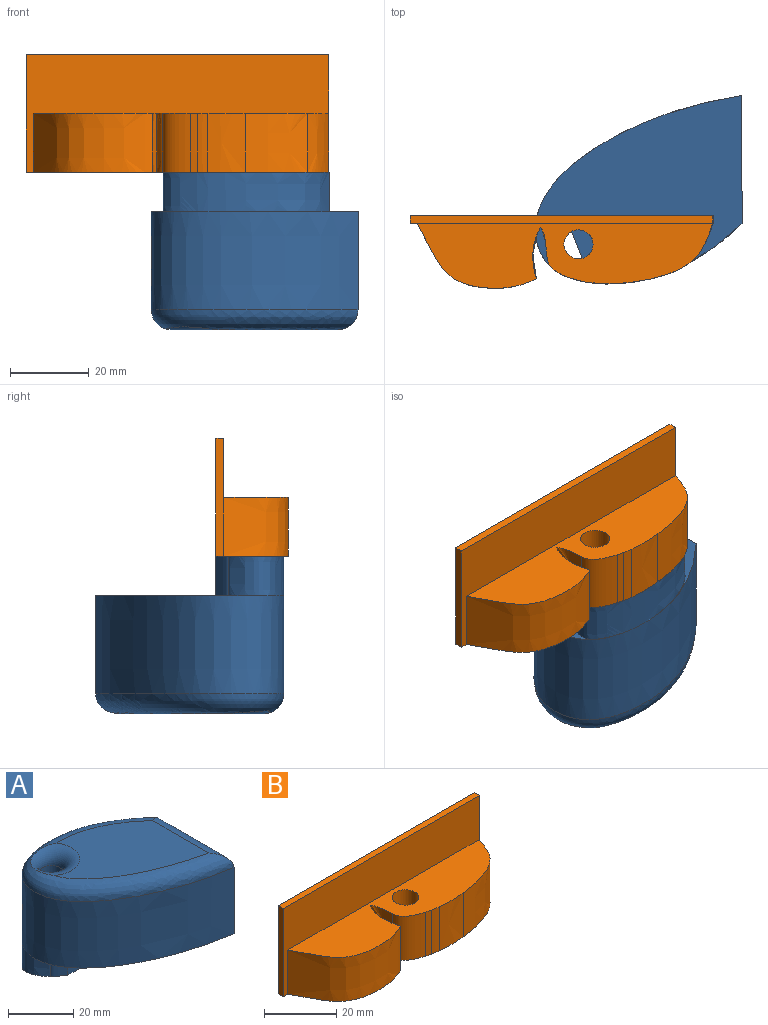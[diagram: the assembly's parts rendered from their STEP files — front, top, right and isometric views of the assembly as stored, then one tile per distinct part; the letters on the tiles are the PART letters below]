
ASSEMBLY  parts=2 mates=1
PART A: 18 faces, bbox 54.8x48.9x40 mm
  f0: plane 54.08x48.92mm, normal (0,0,-1), area 1219.3mm2, adj f1,f3,f4,f15,f16,f17
  f1: extruded ~42.09x15.25mm, area 596.5mm2, adj f0,f2,f10,f13,f14,f15,f16
  f2: plane 2.18x0.61mm, normal (0,0,-1), area 0mm2, adj f1,f4
  f3: plane 32.6x25mm, normal (1,0,0), area 815.1mm2, adj f0,f4,f8
  f4: extruded ~52.55x47.9mm, area 3277.6mm2, adj f0,f2,f3,f9,f10,f14
  f5: cylinder r=3.73mm len=25mm, axis (0,0,-1), area 585.4mm2, adj f7,f11
  f6: plane 42.11x36.98mm, normal (0,0,1), area 913.3mm2, adj f7,f8,f9
  f7: torus R=8.73mm, axis (0,0,1), area 227mm2, adj f5,f6,f9
  f8: cylinder r=5mm len=32.6mm, axis (0,-1,0), area 224.1mm2, adj f3,f6,f9
  f9: bspline ~53.26x47.91mm, area 944.3mm2, adj f4,f6,f7,f8
  f10: plane 2.77x0.58mm, normal (0,0,1), area 0mm2, adj f1,f4
  f11: plane 7.45x7.45mm, normal (0,0,1), area 0.3mm2, adj f5,f12
  f12: cylinder r=3.71mm len=10mm, axis (0,0,1), area 233.3mm2, adj f11,f13
  f13: plane 42.52x17.62mm, normal (0,0,-1), area 540.7mm2, adj f1,f12,f15,f16,f17
  f14: plane 5.89x3.33mm, normal (0,0,1), area 0.4mm2, adj f1,f4
  f15: extruded ~10x4.2mm, area 54.7mm2, adj f0,f1,f13,f17
  f16: plane 10x2mm, normal (1,0,0), area 20mm2, adj f0,f1,f13,f17
  f17: plane 34.25x10mm, normal (0,-1,0), area 342.5mm2, adj f0,f13,f15,f16
PART B: 20 faces, bbox 77x18.6x30 mm
  f0: plane 75.34x16.75mm, normal (0,0,1), area 899.1mm2, adj f1,f2,f3,f4,f5,f6,f7,f8
  f1: extruded ~15x0.02mm, area 0.5mm2, adj f0,f6,f13,f19
  f2: extruded ~30.34x16.47mm, area 581.8mm2, adj f0,f13,f14,f19
  f3: extruded ~15.9x15mm, area 255.1mm2, adj f0,f4,f11,f13
  f4: extruded ~15x9.61mm, area 167.4mm2, adj f0,f3,f13,f17
  f5: extruded ~15x0.1mm, area 1.5mm2, adj f0,f6,f13,f19
  f6: plane 15x8.85mm, normal (0,1,0), area 132.7mm2, adj f0,f1,f5,f13
  f7: extruded ~15x7.28mm, area 113.6mm2, adj f0,f8,f13,f14
  f8: extruded ~15x7.02mm, area 148.1mm2, adj f0,f7,f9,f13
  f9: extruded ~15x1.8mm, area 27.9mm2, adj f0,f8,f10,f13
  f10: extruded ~15x2.64mm, area 40.2mm2, adj f0,f9,f11,f13
  f11: extruded ~15x9.44mm, area 141.9mm2, adj f0,f3,f10,f13
  f12: cylinder r=3.71mm len=15mm, axis (0,0,-1), area 349.9mm2, adj f0,f13
  f13: plane 77x18.61mm, normal (0,0,-1), area 1053.1mm2, adj f1,f2,f3,f4,f5,f6,f7,f8
  f14: extruded ~15x13.04mm, area 202.5mm2, adj f0,f2,f7,f13
  f15: plane 30x2mm, normal (-1,0,0), area 60mm2, adj f13,f16,f18,f19
  f16: plane 77x2mm, normal (0,0,1), area 154mm2, adj f15,f17,f18,f19
  f17: plane 30x2mm, normal (1,0,0), area 60mm2, adj f4,f13,f16,f18,f19
  f18: plane 77x30mm, normal (0,1,0), area 2310mm2, adj f13,f15,f16,f17
  f19: plane 77x30mm, normal (0,-1,0), area 1315.9mm2, adj f0,f1,f2,f5,f13,f15,f16,f17
PLACE A rot(axis=(1,0,0),180deg) t=(6.25,-1.61,-4.19)mm
PLACE B t=(6.26,-1.63,5.81)mm
MATE cylindrical A.f5 <-> B.f12  axis (0,0,1) through (-35.34,-6.87,5.81)mm
